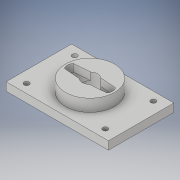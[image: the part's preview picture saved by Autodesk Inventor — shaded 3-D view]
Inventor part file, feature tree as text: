
AUTODESK INVENTOR PART (.ipt)
format: ipt  version: 2017 (Build 210142000, 142)  size: 159,744 bytes
history: native  units: in
note: dims shown in document units (in); Inventor stores cm internally (conversion verified against a paired STEP export)
features: extrude x3, sketch x3
ambient origin geometry x8: Origin, YZ Plane, XZ Plane, XY Plane, X Axis, Y Axis, Z Axis, Center Point
bodies: Solid1 (feature_tree)
feature tree (6):
  extrude  "Extrusion1"  Depth=1.2598in
  extrude  "Extrusion2"  Depth=0.1672in
  extrude  "Extrusion3"  Depth=0.1447in
  sketch  "Sketch1"  dims[d0=1.9685in d1=1.2598in]
  sketch  "Sketch2"  dims[d2=0.2263in d3=0.1672in]
  sketch  "Sketch3"  dims[d4=0.0984in d5=0.2953in d6=0.1575in d7=0.0in d8=0.9449in d9=0.2756in d10=0.2756in d11=0.0591in d12=0.0591in d13=0.0915in d14=0.0in d15=0.0221in d16=0.2756in d17=0.1133in d18=0.1312in d20=0.0896in d21=0.0323in d22=0.1447in d23=0.0in]
